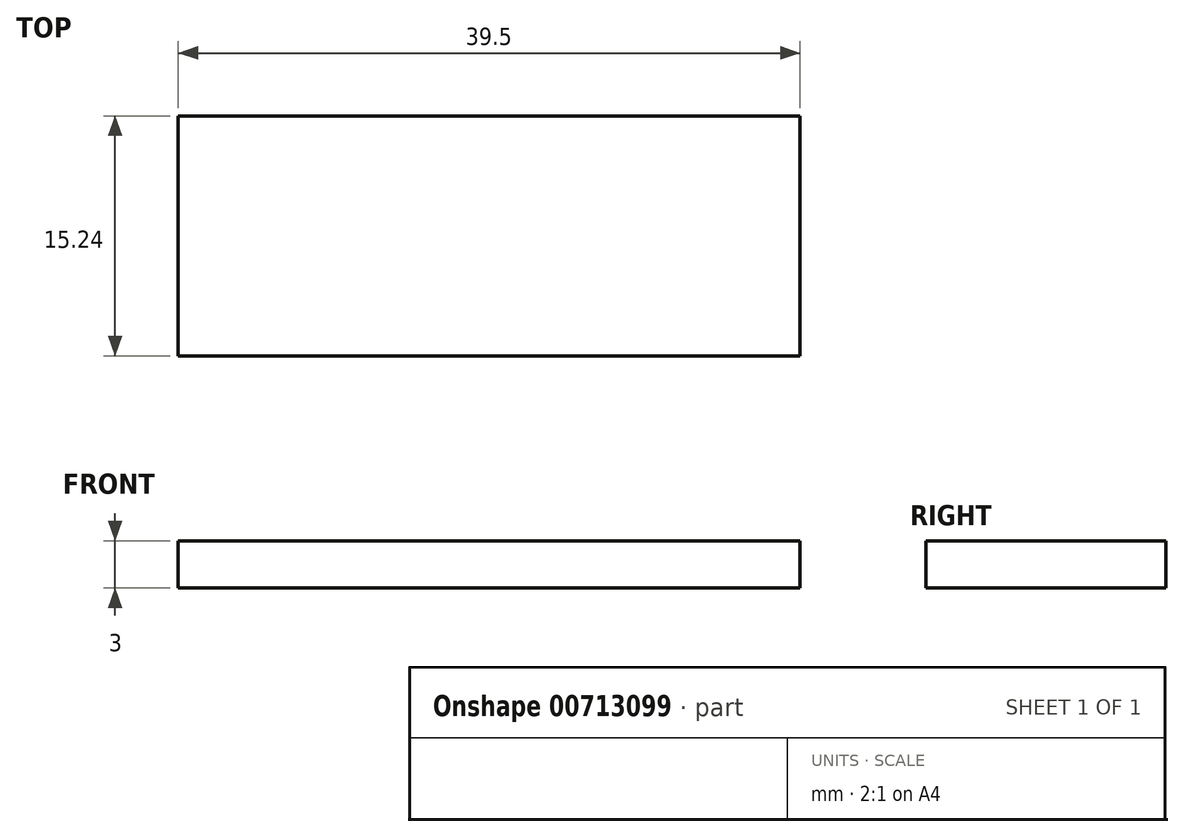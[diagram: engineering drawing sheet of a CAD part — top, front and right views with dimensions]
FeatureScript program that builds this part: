
annotation { "Feature Type Name" : "Feature", "Feature Type Description" : "" }
export const myFeature = defineFeature(function(context is Context, id is Id, definition is map)
    precondition{}
    {
        {
            var Q0;
            Q0=qCreatedBy(makeId("Top.planeOp"),FACE);
            var sketch = newSketch(context, id + "F0", { "sketchPlane" : qUnion([Q0])});
            skLineSegment(sketch, "E0.bottom", {"start": v(13.5, -20) * mm, "end": v(-53, -20) * mm});
            skLineSegment(sketch, "E0.top", {"start": v(13.5, 20) * mm, "end": v(-53, 20) * mm});
            skLineSegment(sketch, "E0.left", {"start": v(13.5, -20) * mm, "end": v(13.5, 20) * mm});
            skLineSegment(sketch, "E0.right", {"start": v(-53, -20) * mm, "end": v(-53, 20) * mm});
            skPoint(sketch, "E0.middle", {"position": v(0, 0) * mm});
            skLineSegment(sketch, "E1.bottom", {"start": v(10, -10) * mm, "end": v(-10, -10) * mm, "construction": true});
            skLineSegment(sketch, "E1.top", {"start": v(10, 10) * mm, "end": v(-10, 10) * mm, "construction": true});
            skLineSegment(sketch, "E1.left", {"start": v(10, -10) * mm, "end": v(10, 10) * mm, "construction": true});
            skLineSegment(sketch, "E1.right", {"start": v(-10, -10) * mm, "end": v(-10, 10) * mm, "construction": true});
            skLineSegment(sketch, "E2", {"start": v(0, 0) * mm, "end": v(0, 0) * mm});
            skLineSegment(sketch, "E3", {"start": v(0, 0) * mm, "end": v(-53, 0) * mm, "construction": true});
            skPoint(sketch, "E4", {"position": v(-24, 0) * mm});
            skPoint(sketch, "E5", {"position": v(-49, 0) * mm});
            skLineSegment(sketch, "E6.bottom", {"start": v(-53, -20) * mm, "end": v(-13.5, -20) * mm});
            skLineSegment(sketch, "E6.top", {"start": v(-53, -4.76) * mm, "end": v(-13.5, -4.76) * mm});
            skLineSegment(sketch, "E6.left", {"start": v(-53, -20) * mm, "end": v(-53, -4.76) * mm});
            skLineSegment(sketch, "E6.right", {"start": v(-13.5, -20) * mm, "end": v(-13.5, -4.76) * mm});
            skLineSegment(sketch, "E7.bottom", {"start": v(-53, 20) * mm, "end": v(-13.5, 20) * mm});
            skLineSegment(sketch, "E7.top", {"start": v(-53, 5.24) * mm, "end": v(-13.5, 5.24) * mm});
            skLineSegment(sketch, "E7.left", {"start": v(-53, 20) * mm, "end": v(-53, 5.24) * mm});
            skLineSegment(sketch, "E7.right", {"start": v(-13.5, 20) * mm, "end": v(-13.5, 5.24) * mm});
            skSolve(sketch);
        }
        {
            var Q0;
            Q0=makeQuery(id+"F0.imprint","IMPRINT",FACE,{"disambiguationData":[TD([[makeQuery(id+"F0.imprint","IMPRINT",EDGE,{"derivedFrom":sQuery(id+"F0.wireOp",EDGE,"E0.bottom")}),-1.0]])]});
            extrude(context, id + "F1", {"entities" : qUnion([Q0]), "depth" : 3 * mm, "offsetDistance" : 25 * mm});
        }
        {
            var Q0;
            Q0=sQuery(id+"F0.wireOp",VERTEX,"E5");
            var Q1;
            Q1=sQuery(id+"F0.wireOp",VERTEX,"E4");
            var Q2;
            Q2=sQuery(id+"F0.wireOp",VERTEX,"E1.right.start");
            var Q3;
            Q3=sQuery(id+"F0.wireOp",VERTEX,"E1.top.start");
            var Q4;
            Q4=sQuery(id+"F0.wireOp",VERTEX,"E1.left.start");
            var Q5;
            Q5=sQuery(id+"F0.wireOp",VERTEX,"E1.top.end");
            var Q6;
            Q6=makeQuery(id+"F1.opExtrude","SWEPT_BODY",BODY,{"disambiguationData":[OSD([sQuery(id+"F0.wireOp",EDGE,"E0.bottom"),sQuery(id+"F0.wireOp",EDGE,"E0.top"),sQuery(id+"F0.wireOp",EDGE,"E0.left"),sQuery(id+"F0.wireOp",EDGE,"E0.right")])]});
            hole(context, id + "F2", {"style" : HoleStyle.SIMPLE, "endStyle" : HoleEndStyle.THROUGH, "oppositeDirection" : true, "holeDiameter" : 4 * mm, "majorDiameter" : 5 * mm, "isTappedThrough" : true, "tappedDepth" : 12 * mm, "tapClearance" : 3, "locations" : qUnion([Q0, Q1, Q2, Q3, Q4, Q5]), "scope" : qUnion([Q6])});
        }
    });
